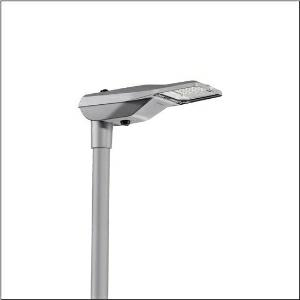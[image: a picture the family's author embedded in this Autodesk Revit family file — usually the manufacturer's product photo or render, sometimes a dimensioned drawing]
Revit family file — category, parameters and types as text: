
# Revit family: streetlight_sl_21_micro___st0_8a_5xe1c43t08db_13be
name_source: partatom
category: Lighting Fixtures
units: mm (PartAtom-declared; Revit-internal decimal feet)

## family parameters
Cut with Voids When Loaded = No
Host = Face
Light Source = No
Part Type = Normal
Room Calculation Point = No
Round Connector Dimension = Use Diameter
Shared = No

## types (1)
- --- (1 x LED, 5320 lm, 39.1 W, 4000K)
    Apparent Load = 39 VA
    CIE Flux Codes = 38 75 97 100 100
    Color Rendering = 70
    Color Temperature = 4000K
    Default Elevation = 1800 mm
    Description = Streetlight SL 21 micro, mast luminaire, primary light control with lens, of PMMA, primary optical cover: cover, of toughened safety glass, transparent, light distribution: ST0.8a, light emission: direct distribution, primary light characteristic: asymmetric, installation type: side-entry, post-top, LED, High Power LED, rated luminous flux: 5.320lm, luminous efficacy: 136lm/W, light colour: 740, colour temperature: 4000K, control gear: D4i, control: flexible luminous flux parameterisation, time-dependent luminous flux control, constant luminous flux control, overheat protection, pre-setting: logarithmic dimming characteristic, mains connection: 220..240V, AC, 50/60Hz, start of lifetime: 39W, end of service life: 41W, reduction: 18W, luminaire housing, of diecast aluminium, powder-coated, Siteco® metallic grey (DB 702S), corrosivity category C5 mid according to DIN EN ISO 12944, please order mast flange separately, inclination adjustable: 0°, 5°, 10°, 15°, sealing non-destructively replaceable, multi-level sealing system, length: 528mm, width: 235mm, height: 110mm, mast flange for spigot size: 42mm (side-entry): 5XC10008XM4, 60/48mm (side-entry/post-top): 5XC10108XM2, 76/60mm (side-entry/post-top): 5XC10108XM1, Smart Interface below and above, protection rating (complete): IP66, insulation class (complete): insulation class II (safety insulation), certification: CE, ENEC, ENEC+, VDE, impact resistance: IK10, permissible operating ambient temperature for outdoor applications: -40..+50°C, standard-compliant lighting for roads and squares, packaging unit: 1 piece

Light Distribution: ST0.8a
    Height = 110 mm
    Lamp = 1 x LED
    Lamp Light Flux = 5320 lm
    Lamp Power = 39.1 W
    Lamp count = 1
    Length = 528 mm
    Luminous efficacy = 136 lm/W
    Manufacturer = Siteco
    ModVariant = No
    Model = 5XE1C43T08DB
    Number of Poles = 1
    OnlyDefault = Yes
    Power Factor = 1
    Product Name = Streetlight SL 21 micro | ST0.8a
    Product group = mast luminaire | pylon top
    ProductGroupID = 6100
    Protection Class = Protection class II
    Protection Degree = IP 66
    RLX_Detail_Level = 1
    RLX_Emergency_Light_Flux = 0 lm
    RLX_Emergency_Type = 0
    RLX_Emergency_Type_DB = No
    RlxData = <blob elided: 98729 chars, md5=2fd87177>
    Socket = socket
    Standby Power = 0 W
    System Light Flux = 5320 lm
    System Power = 39 W
    Type Comments = factory setting: luminous flux: 100 % | dim-lin: 254 | 765 mA
    Type Image = l_1007239.jpg
    URL = http://relux.com
    VarID = @adj_175793
    Voltage = 0 V
    Weight = 0.00 kg
    Width = 235 mm

## geometry (parser evidence)
native form markers: Blend x4, Sweep x10
no freeform markers — native parametric forms only
